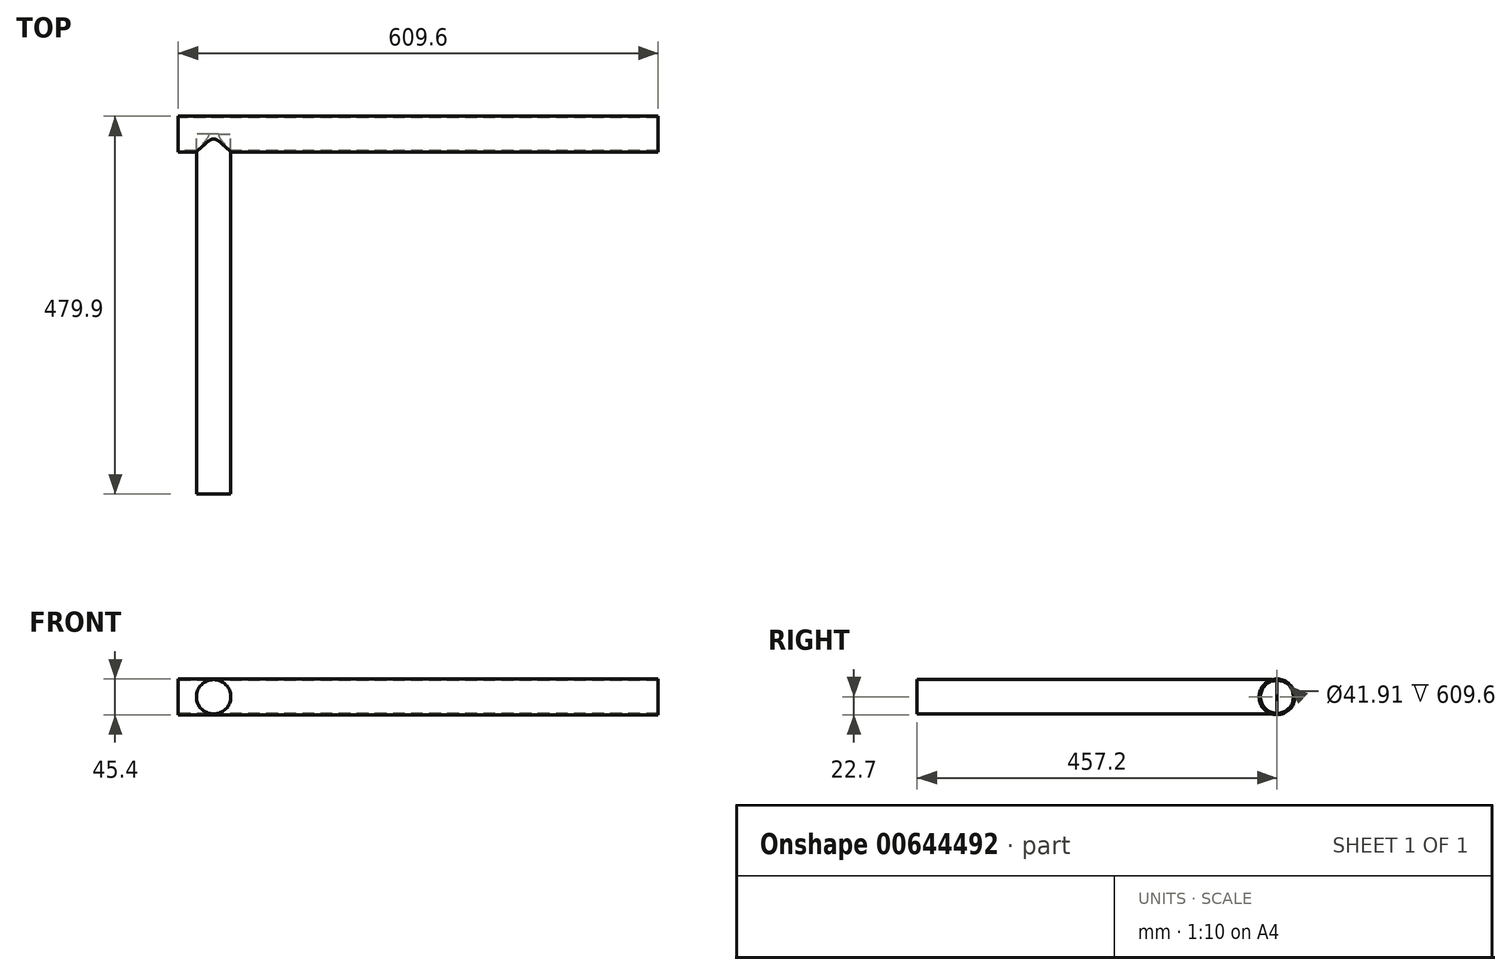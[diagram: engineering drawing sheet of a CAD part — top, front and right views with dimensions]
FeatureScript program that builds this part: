
annotation { "Feature Type Name" : "Feature", "Feature Type Description" : "" }
export const myFeature = defineFeature(function(context is Context, id is Id, definition is map)
    precondition{}
    {
        {
            var Q0;
            Q0=qCreatedBy(makeId("Right.planeOp"),FACE);
            var sketch = newSketch(context, id + "F0", { "sketchPlane" : qUnion([Q0])});
            skCircle(sketch, "E0", {"center": v(0, 0) * mm, "radius": 22.7 * mm});
            skSolve(sketch);
        }
        {
            var Q0;
            Q0=makeQuery(id+"F0.imprint","IMPRINT",FACE,{"disambiguationData":[TD([[makeQuery(id+"F0.imprint","IMPRINT",EDGE,{"derivedFrom":sQuery(id+"F0.wireOp",EDGE,"E0")}),1.0]])]});
            extrude(context, id + "F1", {"entities" : qUnion([Q0]), "depth" : 609.6 * mm, "offsetDistance" : 25.4 * mm});
        }
        {
            var Q0;
            Q0=makeQuery(id+"F1.opExtrude","CAP_FACE",FACE,{"disambiguationData":[OSD([sQuery(id+"F0.wireOp",EDGE,"E0")])],"isStart":true});
            var sketch = newSketch(context, id + "F2", { "sketchPlane" : qUnion([Q0])});
            skCircle(sketch, "E1", {"center": v(0, 0) * mm, "radius": 21.03 * mm});
            skSolve(sketch);
        }
        {
            var Q0;
            Q0=sQuery(id+"F2.wireOp",VERTEX,"E1.center");
            var Q1;
            Q1=makeQuery(id+"F1.opExtrude","SWEPT_BODY",BODY,{"disambiguationData":[OSD([sQuery(id+"F0.wireOp",EDGE,"E0")])]});
            hole(context, id + "F3", {"style" : HoleStyle.SIMPLE, "endStyle" : HoleEndStyle.THROUGH, "holeDiameter" : 41.9 * mm, "majorDiameter" : 15.88 * mm, "isTappedThrough" : true, "tappedDepth" : 12.7 * mm, "tapClearance" : 3, "startFromSketch" : true, "locations" : qUnion([Q0]), "scope" : qUnion([Q1])});
        }
        {
            var Q0;
            Q0=qCreatedBy(makeId("Front.planeOp"),FACE);
            var sketch = newSketch(context, id + "F4", { "sketchPlane" : qUnion([Q0])});
            skCircle(sketch, "E2", {"center": v(44.86, 0) * mm, "radius": 21.83 * mm});
            skSolve(sketch);
        }
        {
            var Q0;
            Q0=makeQuery(id+"F4.imprint","IMPRINT",FACE,{"disambiguationData":[TD([[makeQuery(id+"F4.imprint","IMPRINT",EDGE,{"derivedFrom":sQuery(id+"F4.wireOp",EDGE,"E2")}),1.0]])]});
            extrude(context, id + "F5", {"entities" : qUnion([Q0]), "operationType" : NewBodyOperationType.ADD, "depth" : 457.2 * mm, "offsetDistance" : 25.4 * mm});
        }
    });
